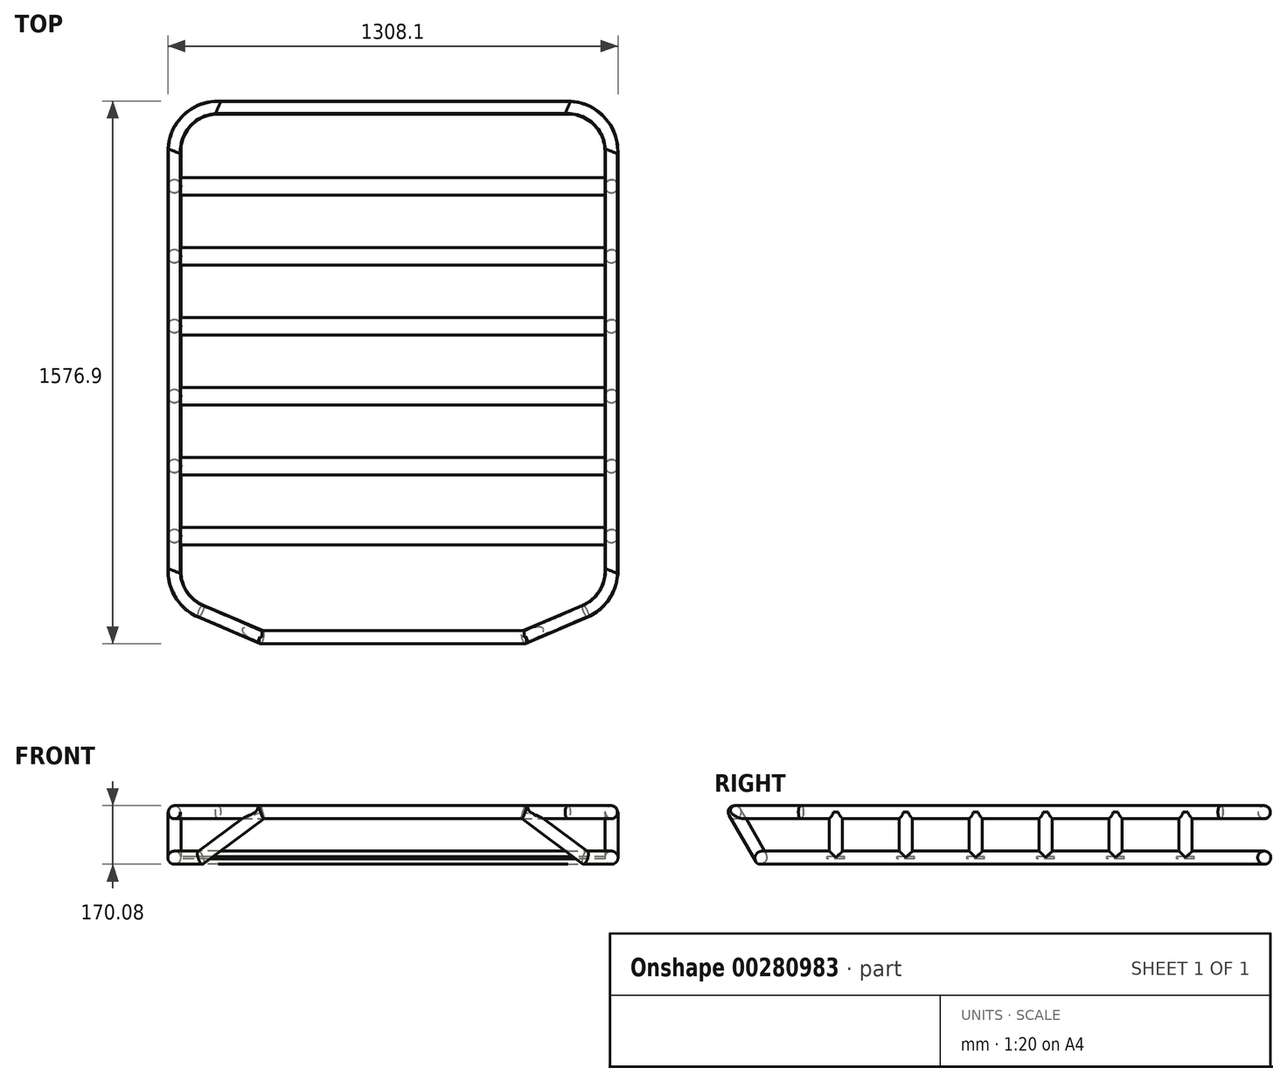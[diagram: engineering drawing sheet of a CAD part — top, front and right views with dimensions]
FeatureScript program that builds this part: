
annotation { "Feature Type Name" : "Feature", "Feature Type Description" : "" }
export const myFeature = defineFeature(function(context is Context, id is Id, definition is map)
    precondition{}
    {
        {
            var Q0;
            Q0=qCreatedBy(makeId("Top.planeOp"),FACE);
            var sketch = newSketch(context, id + "F0", { "sketchPlane" : qUnion([Q0])});
            skLineSegment(sketch, "E0.top", {"start": v(508, 736.6) * mm, "end": v(-508, 736.6) * mm});
            skLineSegment(sketch, "E0.left", {"start": v(635, -609.6) * mm, "end": v(635, 609.6) * mm});
            skLineSegment(sketch, "E0.right", {"start": v(-635, -609.6) * mm, "end": v(-635, 609.6) * mm});
            skPoint(sketch, "E0.middle", {"position": v(0, 0) * mm});
            skPoint(sketch, "E1.visualSharp", {"position": v(-635, 736.6) * mm});
            skArc(sketch, "E1.filletArc", {"start": v(-508, 736.6) * mm, "mid": v(-597.8, 699.4) * mm, "end": v(-635, 609.6) * mm});
            skPoint(sketch, "E2.visualSharp", {"position": v(635, 736.6) * mm});
            skArc(sketch, "E2.filletArc", {"start": v(635, 609.6) * mm, "mid": v(597.8, 699.4) * mm, "end": v(508, 736.6) * mm});
            skPoint(sketch, "E3.visualSharp", {"position": v(635, -736.6) * mm});
            skArc(sketch, "E3.filletArc", {"start": v(558.8, -726) * mm, "mid": v(614.26, -679.16) * mm, "end": v(635, -609.6) * mm});
            skPoint(sketch, "E4.visualSharp", {"position": v(-635, -736.6) * mm});
            skArc(sketch, "E4.filletArc", {"start": v(-635, -609.6) * mm, "mid": v(-614.26, -679.16) * mm, "end": v(-558.8, -726) * mm});
            skPoint(sketch, "E5.middle", {"position": v(0, -1030.73) * mm});
            skPoint(sketch, "E6.middle", {"position": v(0, -796.9) * mm});
            skPoint(sketch, "E7.middle", {"position": v(0, -632.3) * mm});
            skPoint(sketch, "E8.middle", {"position": v(0, -445.4) * mm});
            skSolve(sketch);
        }
        {
            var Q0;
            Q0=sQuery(id+"F0.wireOp",VERTEX,"E3.filletArc.start");
            var Q1;
            Q1=sQuery(id+"F0.wireOp",EDGE,"E0.top");
            cPlane(context, id + "F1", {"entities" : qUnion([Q0, Q1]), "cplaneType" : CPlaneType.LINE_ANGLE, "offset" : 25.4 * mm, "angle" : 240 * degree, "width" : 152.4 * mm, "height" : 152.4 * mm});
        }
        {
            var Q0;
            Q0=qCreatedBy(id+"F1.planeOp",FACE);
            var Q1;
            Q1=sQuery(id+"F0.wireOp",VERTEX,"E3.filletArc.start");
            cPlane(context, id + "F2", {"entities" : qUnion([Q0, Q1]), "cplaneType" : CPlaneType.PLANE_POINT, "offset" : 25.4 * mm, "width" : 152.4 * mm, "height" : 152.4 * mm});
        }
        {
            var Q0;
            Q0=qCreatedBy(id+"F2.planeOp",FACE);
            var sketch = newSketch(context, id + "F3", { "sketchPlane" : qUnion([Q0])});
            skLineSegment(sketch, "E9", {"start": v(558.8, 363) * mm, "end": v(381, 515.4) * mm});
            skLineSegment(sketch, "E10", {"start": v(381, 515.4) * mm, "end": v(0, 515.4) * mm});
            skLineSegment(sketch, "E11", {"start": v(0, 515.4) * mm, "end": v(0, 135.8) * mm, "construction": true});
            skLineSegment(sketch, "E12.MirrorCS", {"start": v(-381, 515.4) * mm, "end": v(0, 515.4) * mm});
            skLineSegment(sketch, "E13.MirrorCS", {"start": v(-558.8, 363) * mm, "end": v(-381, 515.4) * mm});
            skSolve(sketch);
        }
        {
            var Q0;
            Q0=qCreatedBy(makeId("Right.planeOp"),FACE);
            var sketch = newSketch(context, id + "F4", { "sketchPlane" : qUnion([Q0])});
            skCircle(sketch, "E14", {"center": v(-802.2, 131.98) * mm, "radius": 19.05 * mm});
            skSolve(sketch);
        }
        {
            var Q0;
            Q0=makeQuery(id+"F4.imprint","IMPRINT",FACE,{"disambiguationData":[TD([[makeQuery(id+"F4.imprint","IMPRINT",EDGE,{"derivedFrom":sQuery(id+"F4.wireOp",EDGE,"E14")}),1.0]])]});
            var Q1;
            Q1=sQuery(id+"F3.wireOp",EDGE,"E10");
            var Q2;
            Q2=sQuery(id+"F3.wireOp",EDGE,"E9");
            var Q3;
            Q3=sQuery(id+"F0.wireOp",EDGE,"E3.filletArc");
            var Q4;
            Q4=sQuery(id+"F0.wireOp",EDGE,"E0.left");
            var Q5;
            Q5=sQuery(id+"F0.wireOp",EDGE,"E2.filletArc");
            var Q6;
            Q6=sQuery(id+"F0.wireOp",EDGE,"E0.top");
            var Q7;
            Q7=sQuery(id+"F0.wireOp",EDGE,"E1.filletArc");
            var Q8;
            Q8=sQuery(id+"F0.wireOp",EDGE,"E0.right");
            var Q9;
            Q9=sQuery(id+"F0.wireOp",EDGE,"E4.filletArc");
            var Q10;
            Q10=sQuery(id+"F3.wireOp",EDGE,"E13.MirrorCS");
            var Q11;
            Q11=sQuery(id+"F3.wireOp",EDGE,"E12.MirrorCS");
            sweep(context, id + "F5", {"profiles" : qUnion([Q0]), "path" : qUnion([Q1, Q2, Q3, Q4, Q5, Q6, Q7, Q8, Q9, Q10, Q11])});
        }
        {
            var Q0;
            Q0=qCreatedBy(makeId("Right.planeOp"),FACE);
            var Q1;
            Q1=sQuery(id+"F0.wireOp",VERTEX,"E3.filletArc.end");
            cPlane(context, id + "F6", {"entities" : qUnion([Q0, Q1]), "cplaneType" : CPlaneType.PLANE_POINT, "offset" : 25.4 * mm, "width" : 152.4 * mm, "height" : 152.4 * mm});
        }
        {
            var Q0;
            Q0=qCreatedBy(id+"F6.planeOp",FACE);
            var sketch = newSketch(context, id + "F7", { "sketchPlane" : qUnion([Q0])});
            skLineSegment(sketch, "E15", {"start": v(-508, 0) * mm, "end": v(-508, 131.98) * mm});
            skLineSegment(sketch, "E16.1.0.0", {"start": v(-304.8, 0) * mm, "end": v(-304.8, 131.98) * mm});
            skLineSegment(sketch, "E16.2.0.0", {"start": v(-101.6, 0) * mm, "end": v(-101.6, 131.98) * mm});
            skLineSegment(sketch, "E16.3.0.0", {"start": v(101.6, 0) * mm, "end": v(101.6, 131.98) * mm});
            skLineSegment(sketch, "E16.4.0.0", {"start": v(304.8, 0) * mm, "end": v(304.8, 131.98) * mm});
            skLineSegment(sketch, "E16.5.0.0", {"start": v(508, 0) * mm, "end": v(508, 131.98) * mm});
            skLineSegment(sketch, "E16.direction1", {"start": v(-508, 0) * mm, "end": v(-304.8, 0) * mm, "construction": true});
            skSolve(sketch);
        }
        {
            var Q0;
            Q0=qCreatedBy(makeId("Top.planeOp"),FACE);
            var Q1;
            Q1=sQuery(id+"F7.wireOp",VERTEX,"E16.3.0.0.end");
            cPlane(context, id + "F8", {"entities" : qUnion([Q0, Q1]), "cplaneType" : CPlaneType.PLANE_POINT, "offset" : 25.4 * mm, "width" : 152.4 * mm, "height" : 152.4 * mm});
        }
        {
            var Q0;
            Q0=qCreatedBy(id+"F8.planeOp",FACE);
            var sketch = newSketch(context, id + "F9", { "sketchPlane" : qUnion([Q0])});
            skCircle(sketch, "E17", {"center": v(635, -508) * mm, "radius": 19.05 * mm});
            skCircle(sketch, "E18.0.1.0", {"center": v(635, -304.8) * mm, "radius": 19.05 * mm});
            skCircle(sketch, "E18.0.2.0", {"center": v(635, -101.6) * mm, "radius": 19.05 * mm});
            skCircle(sketch, "E18.0.3.0", {"center": v(635, 101.6) * mm, "radius": 19.05 * mm});
            skCircle(sketch, "E18.0.4.0", {"center": v(635, 304.8) * mm, "radius": 19.05 * mm});
            skCircle(sketch, "E18.0.5.0", {"center": v(635, 508) * mm, "radius": 19.05 * mm});
            skLineSegment(sketch, "E18.direction1", {"start": v(635, -508) * mm, "end": v(660.4, -508) * mm, "construction": true});
            skLineSegment(sketch, "E18.direction2", {"start": v(635, -508) * mm, "end": v(635, -304.8) * mm, "construction": true});
            skSolve(sketch);
        }
        {
            var Q0;
            Q0=makeQuery(id+"F9.imprint","IMPRINT",FACE,{"disambiguationData":[TD([[makeQuery(id+"F9.imprint","IMPRINT",EDGE,{"derivedFrom":sQuery(id+"F9.wireOp",EDGE,"E17")}),1.0]])]});
            var Q1;
            Q1=makeQuery(id+"F9.imprint","IMPRINT",FACE,{"disambiguationData":[TD([[makeQuery(id+"F9.imprint","IMPRINT",EDGE,{"derivedFrom":sQuery(id+"F9.wireOp",EDGE,"E18.0.1.0")}),1.0]])]});
            var Q2;
            Q2=makeQuery(id+"F9.imprint","IMPRINT",FACE,{"disambiguationData":[TD([[makeQuery(id+"F9.imprint","IMPRINT",EDGE,{"derivedFrom":sQuery(id+"F9.wireOp",EDGE,"E18.0.2.0")}),1.0]])]});
            var Q3;
            Q3=makeQuery(id+"F9.imprint","IMPRINT",FACE,{"disambiguationData":[TD([[makeQuery(id+"F9.imprint","IMPRINT",EDGE,{"derivedFrom":sQuery(id+"F9.wireOp",EDGE,"E18.0.3.0")}),1.0]])]});
            var Q4;
            Q4=makeQuery(id+"F9.imprint","IMPRINT",FACE,{"disambiguationData":[TD([[makeQuery(id+"F9.imprint","IMPRINT",EDGE,{"derivedFrom":sQuery(id+"F9.wireOp",EDGE,"E18.0.4.0")}),1.0]])]});
            var Q5;
            Q5=makeQuery(id+"F9.imprint","IMPRINT",FACE,{"disambiguationData":[TD([[makeQuery(id+"F9.imprint","IMPRINT",EDGE,{"derivedFrom":sQuery(id+"F9.wireOp",EDGE,"E18.0.5.0")}),1.0]])]});
            var Q6;
            Q6=sQuery(id+"F7.wireOp",EDGE,"E16.5.0.0");
            sweep(context, id + "F10", {"profiles" : qUnion([Q0, Q1, Q2, Q3, Q4, Q5]), "path" : qUnion([Q6])});
        }
        {
            var Q0;
            Q0=makeQuery(id+"F10.opSweep","SWEPT_BODY",BODY,{"disambiguationData":[OSD([sQuery(id+"F7.wireOp",EDGE,"E16.5.0.0"),sQuery(id+"F9.wireOp",EDGE,"E17")])]});
            var Q1;
            Q1=makeQuery(id+"F10.opSweep","SWEPT_BODY",BODY,{"disambiguationData":[OSD([sQuery(id+"F7.wireOp",EDGE,"E16.5.0.0"),sQuery(id+"F9.wireOp",EDGE,"E18.0.1.0")])]});
            var Q2;
            Q2=makeQuery(id+"F10.opSweep","SWEPT_BODY",BODY,{"disambiguationData":[OSD([sQuery(id+"F7.wireOp",EDGE,"E16.5.0.0"),sQuery(id+"F9.wireOp",EDGE,"E18.0.2.0")])]});
            var Q3;
            Q3=makeQuery(id+"F10.opSweep","SWEPT_BODY",BODY,{"disambiguationData":[OSD([sQuery(id+"F7.wireOp",EDGE,"E16.5.0.0"),sQuery(id+"F9.wireOp",EDGE,"E18.0.3.0")])]});
            var Q4;
            Q4=makeQuery(id+"F10.opSweep","SWEPT_BODY",BODY,{"disambiguationData":[OSD([sQuery(id+"F7.wireOp",EDGE,"E16.5.0.0"),sQuery(id+"F9.wireOp",EDGE,"E18.0.4.0")])]});
            var Q5;
            Q5=makeQuery(id+"F10.opSweep","SWEPT_BODY",BODY,{"disambiguationData":[OSD([sQuery(id+"F7.wireOp",EDGE,"E16.5.0.0"),sQuery(id+"F9.wireOp",EDGE,"E18.0.5.0")])]});
            var Q6;
            Q6=qCreatedBy(makeId("Right.planeOp"),FACE);
            mirror(context, id + "F11", {"operationType" : NewBodyOperationType.ADD, "entities" : qUnion([Q0, Q1, Q2, Q3, Q4, Q5]), "mirrorPlane" : qUnion([Q6])});
        }
        {
            var Q0;
            Q0=qCreatedBy(makeId("Top.planeOp"),FACE);
            var Q1;
            Q1=sQuery(id+"F3.wireOp",VERTEX,"E13.MirrorCS.end");
            cPlane(context, id + "F12", {"entities" : qUnion([Q0, Q1]), "cplaneType" : CPlaneType.PLANE_POINT, "offset" : 25.4 * mm, "width" : 152.4 * mm, "height" : 152.4 * mm});
        }
        {
            var Q0;
            Q0=qCreatedBy(id+"F12.planeOp",FACE);
            var sketch = newSketch(context, id + "F13", { "sketchPlane" : qUnion([Q0])});
            skLineSegment(sketch, "E19.0", {"start": v(558.8, -726) * mm, "end": v(381, -802.2) * mm});
            skLineSegment(sketch, "E19.1", {"start": v(635, -609.6) * mm, "end": v(635, 609.6) * mm});
            skArc(sketch, "E19.2", {"start": v(558.8, -726) * mm, "mid": v(614.26, -679.16) * mm, "end": v(635, -609.6) * mm});
            skLineSegment(sketch, "E19.4", {"start": v(508, 736.6) * mm, "end": v(-508, 736.6) * mm});
            skArc(sketch, "E19.5", {"start": v(635, 609.6) * mm, "mid": v(597.8, 699.4) * mm, "end": v(508, 736.6) * mm});
            skArc(sketch, "E19.6", {"start": v(-635, -609.6) * mm, "mid": v(-614.26, -679.16) * mm, "end": v(-558.8, -726) * mm});
            skArc(sketch, "E19.7", {"start": v(-508, 736.6) * mm, "mid": v(-597.8, 699.4) * mm, "end": v(-635, 609.6) * mm});
            skLineSegment(sketch, "E19.9", {"start": v(-635, -609.6) * mm, "end": v(-635, 609.6) * mm});
            skLineSegment(sketch, "E19.10", {"start": v(-558.8, -726) * mm, "end": v(-381, -802.2) * mm});
            skSolve(sketch);
        }
        {
            var Q0;
            Q0=qCreatedBy(makeId("Right.planeOp"),FACE);
            var Q1;
            Q1=sQuery(id+"F3.wireOp",VERTEX,"E10.start");
            cPlane(context, id + "F14", {"entities" : qUnion([Q0, Q1]), "cplaneType" : CPlaneType.PLANE_POINT, "offset" : 25.4 * mm, "width" : 152.4 * mm, "height" : 152.4 * mm});
        }
        {
            var Q0;
            Q0=qCreatedBy(id+"F14.planeOp",FACE);
            var sketch = newSketch(context, id + "F15", { "sketchPlane" : qUnion([Q0])});
            skCircle(sketch, "E20", {"center": v(-802.2, 131.98) * mm, "radius": 19.05 * mm});
            skSolve(sketch);
        }
        {
            var Q0;
            Q0=makeQuery(id+"F15.imprint","IMPRINT",FACE,{"disambiguationData":[TD([[makeQuery(id+"F15.imprint","IMPRINT",EDGE,{"derivedFrom":sQuery(id+"F15.wireOp",EDGE,"E20")}),1.0]])]});
            var Q1;
            Q1=sQuery(id+"F13.wireOp",EDGE,"E19.0");
            var Q2;
            Q2=sQuery(id+"F13.wireOp",EDGE,"E19.2");
            var Q3;
            Q3=sQuery(id+"F13.wireOp",EDGE,"E19.1");
            var Q4;
            Q4=sQuery(id+"F13.wireOp",EDGE,"E19.5");
            var Q5;
            Q5=sQuery(id+"F13.wireOp",EDGE,"E19.4");
            var Q6;
            Q6=sQuery(id+"F13.wireOp",EDGE,"E19.7");
            var Q7;
            Q7=sQuery(id+"F13.wireOp",EDGE,"E19.9");
            var Q8;
            Q8=sQuery(id+"F13.wireOp",EDGE,"E19.6");
            var Q9;
            Q9=sQuery(id+"F13.wireOp",EDGE,"E19.10");
            sweep(context, id + "F16", {"operationType" : NewBodyOperationType.ADD, "profiles" : qUnion([Q0]), "path" : qUnion([Q1, Q2, Q3, Q4, Q5, Q6, Q7, Q8, Q9])});
        }
        {
            var Q0;
            Q0=qCreatedBy(makeId("Top.planeOp"),FACE);
            var sketch = newSketch(context, id + "F17", { "sketchPlane" : qUnion([Q0])});
            skLineSegment(sketch, "E21", {"start": v(635, 508) * mm, "end": v(-369.38, 508) * mm, "construction": true});
            skLineSegment(sketch, "E22", {"start": v(635, 304.8) * mm, "end": v(-365.62, 304.8) * mm, "construction": true});
            skLineSegment(sketch, "E23", {"start": v(635, 101.6) * mm, "end": v(-346.92, 101.6) * mm, "construction": true});
            skLineSegment(sketch, "E24", {"start": v(635, -101.6) * mm, "end": v(-429.68, -101.6) * mm, "construction": true});
            skLineSegment(sketch, "E25", {"start": v(635, -304.8) * mm, "end": v(-420.66, -304.8) * mm, "construction": true});
            skLineSegment(sketch, "E26", {"start": v(635, -508) * mm, "end": v(-384.72, -508) * mm, "construction": true});
            skLineSegment(sketch, "E27.bottom", {"start": v(635, 482.6) * mm, "end": v(-635, 482.6) * mm});
            skLineSegment(sketch, "E27.top", {"start": v(635, 533.4) * mm, "end": v(-635, 533.4) * mm});
            skLineSegment(sketch, "E27.left", {"start": v(635, 482.6) * mm, "end": v(635, 533.4) * mm});
            skLineSegment(sketch, "E27.right", {"start": v(-635, 482.6) * mm, "end": v(-635, 533.4) * mm});
            skPoint(sketch, "E27.middle", {"position": v(0, 508) * mm});
            skLineSegment(sketch, "E28.0.1.0", {"start": v(635, 279.4) * mm, "end": v(-635, 279.4) * mm});
            skLineSegment(sketch, "E28.0.1.1", {"start": v(635, 279.4) * mm, "end": v(635, 330.2) * mm});
            skLineSegment(sketch, "E28.0.1.2", {"start": v(-635, 279.4) * mm, "end": v(-635, 330.2) * mm});
            skLineSegment(sketch, "E28.0.1.3", {"start": v(635, 330.2) * mm, "end": v(-635, 330.2) * mm});
            skLineSegment(sketch, "E28.0.2.0", {"start": v(635, 76.2) * mm, "end": v(-635, 76.2) * mm});
            skLineSegment(sketch, "E28.0.2.1", {"start": v(635, 76.2) * mm, "end": v(635, 127) * mm});
            skLineSegment(sketch, "E28.0.2.2", {"start": v(-635, 76.2) * mm, "end": v(-635, 127) * mm});
            skLineSegment(sketch, "E28.0.2.3", {"start": v(635, 127) * mm, "end": v(-635, 127) * mm});
            skLineSegment(sketch, "E28.0.3.0", {"start": v(635, -127) * mm, "end": v(-635, -127) * mm});
            skLineSegment(sketch, "E28.0.3.1", {"start": v(635, -127) * mm, "end": v(635, -76.2) * mm});
            skLineSegment(sketch, "E28.0.3.2", {"start": v(-635, -127) * mm, "end": v(-635, -76.2) * mm});
            skLineSegment(sketch, "E28.0.3.3", {"start": v(635, -76.2) * mm, "end": v(-635, -76.2) * mm});
            skLineSegment(sketch, "E28.0.4.0", {"start": v(635, -330.2) * mm, "end": v(-635, -330.2) * mm});
            skLineSegment(sketch, "E28.0.4.1", {"start": v(635, -330.2) * mm, "end": v(635, -279.4) * mm});
            skLineSegment(sketch, "E28.0.4.2", {"start": v(-635, -330.2) * mm, "end": v(-635, -279.4) * mm});
            skLineSegment(sketch, "E28.0.4.3", {"start": v(635, -279.4) * mm, "end": v(-635, -279.4) * mm});
            skLineSegment(sketch, "E28.0.5.0", {"start": v(635, -533.4) * mm, "end": v(-635, -533.4) * mm});
            skLineSegment(sketch, "E28.0.5.1", {"start": v(635, -533.4) * mm, "end": v(635, -482.6) * mm});
            skLineSegment(sketch, "E28.0.5.2", {"start": v(-635, -533.4) * mm, "end": v(-635, -482.6) * mm});
            skLineSegment(sketch, "E28.0.5.3", {"start": v(635, -482.6) * mm, "end": v(-635, -482.6) * mm});
            skLineSegment(sketch, "E28.direction1", {"start": v(-635, 533.4) * mm, "end": v(-609.6, 533.4) * mm, "construction": true});
            skLineSegment(sketch, "E28.direction2", {"start": v(-635, 533.4) * mm, "end": v(-635, 330.2) * mm, "construction": true});
            skSolve(sketch);
        }
        {
            var Q0;
            Q0 = qSketchRegion(id + "F17", true);
            extrude(context, id + "F18", {"entities" : qUnion([Q0]), "operationType" : NewBodyOperationType.ADD, "endBound" : BoundingType.SYMMETRIC, "depth" : 6.35 * mm});
        }
    });
